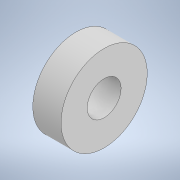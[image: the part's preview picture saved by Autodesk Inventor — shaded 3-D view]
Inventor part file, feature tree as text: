
AUTODESK INVENTOR PART (.ipt)
format: ipt  version: 2022 (Build 260153000, 153)  size: 98,304 bytes
history: native  units: mm
features: extrude x1, sketch x1
ambient origin geometry x8: Origin, YZ Plane, XZ Plane, XY Plane, X Axis, Y Axis, Z Axis, Center Point
bodies: Solid1 (feature_tree)
feature tree (2):
  extrude  "Extrusion1"  Depth=10.0mm
  sketch  "Sketch1"  dims[d0=12.0mm d1=30.5mm d2=10.0mm d3=0.0mm]
